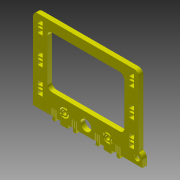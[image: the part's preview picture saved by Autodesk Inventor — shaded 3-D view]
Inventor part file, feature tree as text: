
AUTODESK INVENTOR PART (.ipt)
format: ipt  version: 2012 SP1 (Build 160190100, 190)  size: 620,032 bytes
history: native  units: in
note: dims shown in document units (in); Inventor stores cm internally (conversion verified against a paired STEP export)
features: other x6, extrude x3
ambient origin geometry x8: Origin, YZ Plane, XZ Plane, XY Plane, X Axis, Y Axis, Z Axis, Center Point
bodies: Solid1 (feature_tree)
feature tree (9):
  other  "skeleton.ipt"
  other  "DRILL-THROUGH"
  other  "POCKET_1-16"
  other  "POCKET_3-8"
  other  "STOCK_12MM"
  extrude  "Extrusion1"  Depth=0.3937in
  extrude  "Extrusion2"  Depth=0.4724in
  extrude  "Extrusion3"  TaperAngle=0.0deg  [1 undecoded]
  other  "THROUGH-CUT"
note: 1 required parameter value undecoded (feature->parameter linkage not recoverable at this tier; creation-order binding heuristic only, values carry confidence <= 0.55)
